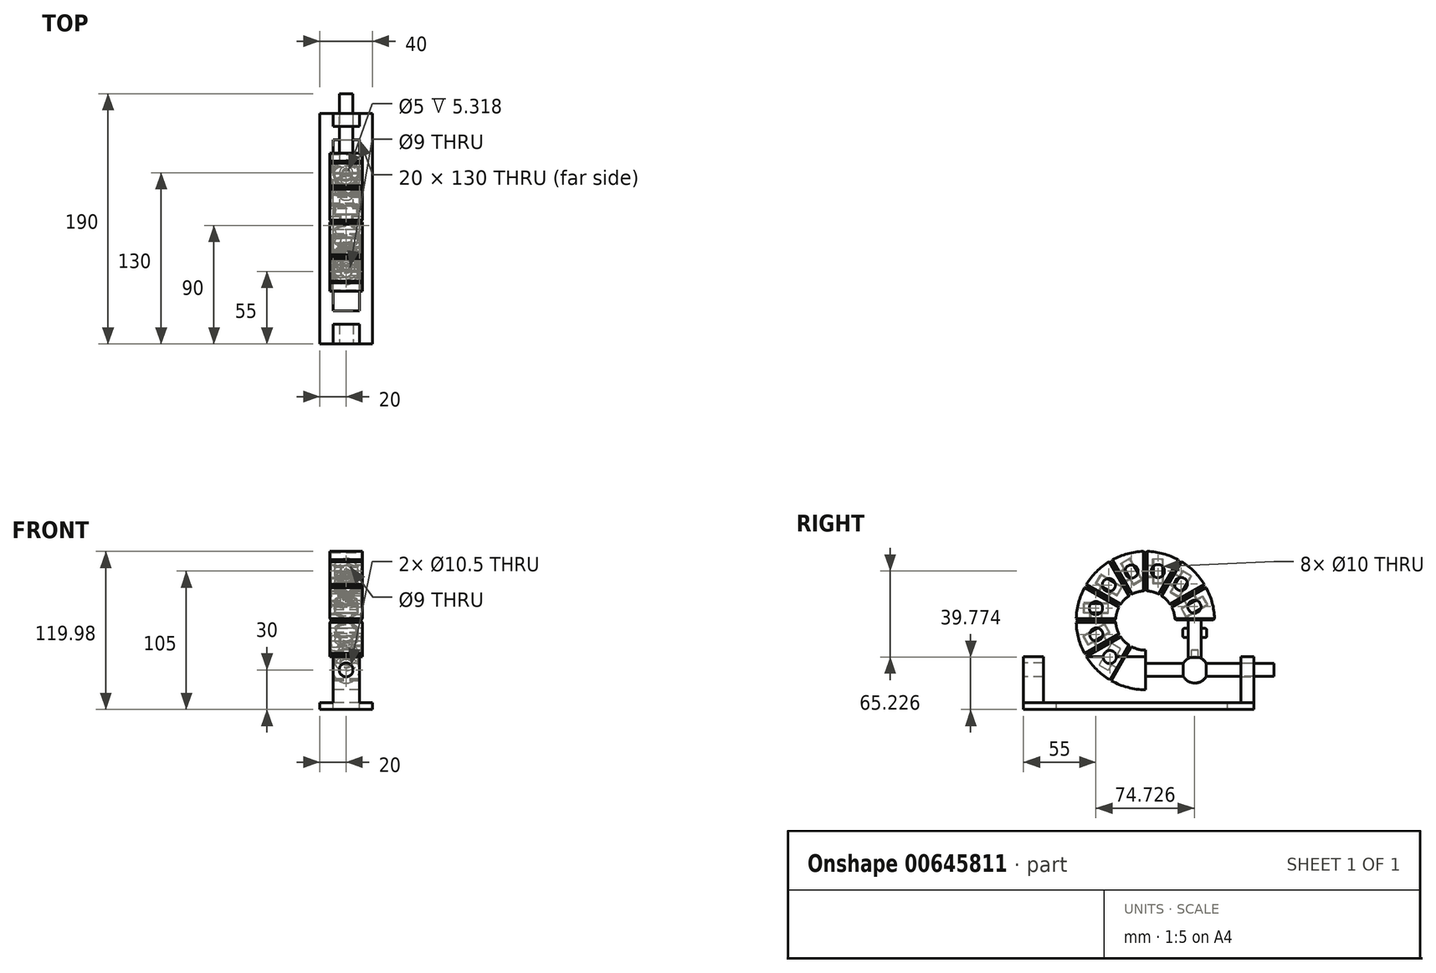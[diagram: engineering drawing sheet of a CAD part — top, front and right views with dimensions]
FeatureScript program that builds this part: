
annotation { "Feature Type Name" : "Feature", "Feature Type Description" : "" }
export const myFeature = defineFeature(function(context is Context, id is Id, definition is map)
    precondition{}
    {
        {
            var Q0;
            Q0=qCreatedBy(makeId("Right.planeOp"),FACE);
            var sketch = newSketch(context, id + "F0", { "sketchPlane" : qUnion([Q0])});
            skLineSegment(sketch, "E0", {"start": v(0, 30) * mm, "end": v(0, 0) * mm});
            skArc(sketch, "E1", {"start": v(-26.25, 7.03) * mm, "mid": v(-13.59, 1.79) * mm, "end": v(0, 0) * mm});
            skArc(sketch, "E2", {"start": v(0, 30) * mm, "mid": v(-5.82, 30.77) * mm, "end": v(-11.25, 33.01) * mm});
            skLineSegment(sketch, "E3", {"start": v(-11.25, 33.01) * mm, "end": v(-26.25, 7.03) * mm, "construction": true});
            skLineSegment(sketch, "E4", {"start": v(-16.32, 23.24) * mm, "end": v(-21.95, 26.49) * mm});
            skLineSegment(sketch, "E5", {"start": v(-25.95, 19.56) * mm, "end": v(-20.32, 16.3) * mm});
            skLineSegment(sketch, "E6", {"start": v(-25.95, 19.56) * mm, "end": v(-27.95, 16.1) * mm});
            skLineSegment(sketch, "E7", {"start": v(-29.31, 15.73) * mm, "end": v(-33.64, 18.23) * mm});
            skLineSegment(sketch, "E8", {"start": v(-34, 19.6) * mm, "end": v(-26, 33.45) * mm});
            skLineSegment(sketch, "E9", {"start": v(-24.64, 33.82) * mm, "end": v(-20.31, 31.32) * mm});
            skLineSegment(sketch, "E10", {"start": v(-19.95, 29.95) * mm, "end": v(-21.95, 26.49) * mm});
            skLineSegment(sketch, "E11", {"start": v(-18.75, 20.02) * mm, "end": v(-30.44, 26.77) * mm});
            skArc(sketch, "E12.MirrorCS", {"start": v(-19.49, 41.25) * mm, "mid": v(-15.9, 36.6) * mm, "end": v(-11.25, 33.01) * mm});
            skLineSegment(sketch, "E13.MirrorCS", {"start": v(-19.49, 41.25) * mm, "end": v(-45.47, 26.25) * mm});
            skArc(sketch, "E14.MirrorCS", {"start": v(-26.25, 7.03) * mm, "mid": v(-37.12, 15.38) * mm, "end": v(-45.47, 26.25) * mm});
            skLineSegment(sketch, "E15", {"start": v(-11.68, 33.27) * mm, "end": v(-16.43, 25.04) * mm});
            skLineSegment(sketch, "E16.MirrorCS", {"start": v(-26.69, 7.28) * mm, "end": v(-21.93, 15.51) * mm});
            skLineSegment(sketch, "E17", {"start": v(-25.82, 6.78) * mm, "end": v(-10.81, 32.77) * mm});
            skLineSegment(sketch, "E18", {"start": v(-22.3, 16.88) * mm, "end": v(-24.9, 18.38) * mm});
            skLineSegment(sketch, "E19", {"start": v(-26.26, 18.01) * mm, "end": v(-28.26, 14.55) * mm});
            skLineSegment(sketch, "E20", {"start": v(-28.26, 14.55) * mm, "end": v(-35.2, 18.55) * mm});
            skLineSegment(sketch, "E21", {"start": v(-35.2, 18.55) * mm, "end": v(-25.7, 35) * mm});
            skLineSegment(sketch, "E22", {"start": v(-25.7, 35) * mm, "end": v(-18.76, 31) * mm});
            skLineSegment(sketch, "E23", {"start": v(-18.76, 31) * mm, "end": v(-20.76, 27.54) * mm});
            skLineSegment(sketch, "E24", {"start": v(-20.4, 26.17) * mm, "end": v(-17.8, 24.67) * mm});
            skLineSegment(sketch, "E25", {"start": v(0, 52.5) * mm, "end": v(-39.54, 12.96) * mm, "construction": true});
            skArc(sketch, "E26.1.21", {"start": v(-11.25, 33.01) * mm, "mid": v(-15.9, 36.6) * mm, "end": v(-19.49, 41.25) * mm});
            skPoint(sketch, "E27.orphan", {"position": v(-16.75, 23.49) * mm});
            skPoint(sketch, "E28.orphan", {"position": v(-20.75, 16.56) * mm});
            skLineSegment(sketch, "E29.1.0", {"start": v(-37.12, 32.8) * mm, "end": v(-38.62, 35.4) * mm});
            skLineSegment(sketch, "E29.1.1", {"start": v(-39.99, 35.76) * mm, "end": v(-43.45, 33.76) * mm});
            skLineSegment(sketch, "E29.1.2", {"start": v(-43.45, 33.76) * mm, "end": v(-47.45, 40.7) * mm});
            skLineSegment(sketch, "E29.1.3", {"start": v(-47.45, 40.7) * mm, "end": v(-31, 50.2) * mm});
            skLineSegment(sketch, "E29.1.4", {"start": v(-31, 50.2) * mm, "end": v(-27, 43.26) * mm});
            skLineSegment(sketch, "E29.1.5", {"start": v(-27, 43.26) * mm, "end": v(-30.46, 41.26) * mm});
            skLineSegment(sketch, "E29.1.6", {"start": v(-30.83, 39.9) * mm, "end": v(-29.33, 37.3) * mm});
            skLineSegment(sketch, "E29.1.7", {"start": v(-19.73, 41.69) * mm, "end": v(-27.96, 36.93) * mm});
            skLineSegment(sketch, "E29.1.8", {"start": v(-45.72, 26.68) * mm, "end": v(-37.49, 31.43) * mm});
            skArc(sketch, "E29.1.9", {"start": v(-45.47, 26.25) * mm, "mid": v(-50.71, 38.91) * mm, "end": v(-52.5, 52.5) * mm});
            skArc(sketch, "E29.1.10", {"start": v(-19.49, 41.25) * mm, "mid": v(-21.73, 46.68) * mm, "end": v(-22.5, 52.5) * mm});
            skLineSegment(sketch, "E29.1.11", {"start": v(-45.22, 25.81) * mm, "end": v(-19.23, 40.82) * mm});
            skLineSegment(sketch, "E29.1.12", {"start": v(-22.5, 52.5) * mm, "end": v(-52.5, 52.5) * mm});
            skLineSegment(sketch, "E29.1.13", {"start": v(-30.68, 48.64) * mm, "end": v(-28.18, 44.31) * mm});
            skLineSegment(sketch, "E29.1.14", {"start": v(-45.9, 41) * mm, "end": v(-32.05, 49) * mm});
            skLineSegment(sketch, "E29.1.15", {"start": v(-43.77, 35.31) * mm, "end": v(-46.27, 39.64) * mm});
            skLineSegment(sketch, "E29.1.16", {"start": v(-38.94, 36.95) * mm, "end": v(-42.4, 34.95) * mm});
            skLineSegment(sketch, "E29.1.17", {"start": v(-38.94, 36.95) * mm, "end": v(-35.7, 31.32) * mm});
            skLineSegment(sketch, "E29.1.18", {"start": v(-28.76, 35.32) * mm, "end": v(-32.01, 40.95) * mm});
            skLineSegment(sketch, "E29.1.19", {"start": v(-28.55, 42.95) * mm, "end": v(-32.01, 40.95) * mm});
            skLineSegment(sketch, "E29.2.0", {"start": v(-42, 53) * mm, "end": v(-42, 58) * mm});
            skLineSegment(sketch, "E29.2.1", {"start": v(-42, 58) * mm, "end": v(-47, 58) * mm});
            skLineSegment(sketch, "E29.2.2", {"start": v(-47, 58) * mm, "end": v(-47, 66) * mm});
            skLineSegment(sketch, "E29.2.3", {"start": v(-47, 66) * mm, "end": v(-28, 66) * mm});
            skLineSegment(sketch, "E29.2.4", {"start": v(-28, 66) * mm, "end": v(-28, 58) * mm});
            skLineSegment(sketch, "E29.2.5", {"start": v(-28, 58) * mm, "end": v(-33, 58) * mm});
            skLineSegment(sketch, "E29.2.6", {"start": v(-33, 58) * mm, "end": v(-33, 53) * mm});
            skLineSegment(sketch, "E29.2.7", {"start": v(-22.5, 53) * mm, "end": v(-33, 53) * mm});
            skLineSegment(sketch, "E29.2.8", {"start": v(-52.5, 53) * mm, "end": v(-42, 53) * mm});
            skArc(sketch, "E29.2.9", {"start": v(-52.5, 52.5) * mm, "mid": v(-50.71, 66.09) * mm, "end": v(-45.47, 78.75) * mm});
            skArc(sketch, "E29.2.10", {"start": v(-22.5, 52.5) * mm, "mid": v(-21.73, 58.32) * mm, "end": v(-19.49, 63.75) * mm});
            skLineSegment(sketch, "E29.2.11", {"start": v(-52.5, 52) * mm, "end": v(-22.5, 52) * mm});
            skLineSegment(sketch, "E29.2.12", {"start": v(-19.49, 63.75) * mm, "end": v(-45.47, 78.75) * mm});
            skLineSegment(sketch, "E29.2.13", {"start": v(-28.5, 65.5) * mm, "end": v(-28.5, 58.5) * mm});
            skLineSegment(sketch, "E29.2.14", {"start": v(-46.5, 65.5) * mm, "end": v(-28.5, 65.5) * mm});
            skLineSegment(sketch, "E29.2.15", {"start": v(-46.5, 58.5) * mm, "end": v(-46.5, 65.5) * mm});
            skLineSegment(sketch, "E29.2.16", {"start": v(-41.5, 58.5) * mm, "end": v(-46.5, 58.5) * mm});
            skLineSegment(sketch, "E29.2.17", {"start": v(-41.5, 58.5) * mm, "end": v(-41.5, 52) * mm});
            skLineSegment(sketch, "E29.2.18", {"start": v(-33.5, 52) * mm, "end": v(-33.5, 58.5) * mm});
            skLineSegment(sketch, "E29.2.19", {"start": v(-28.5, 58.5) * mm, "end": v(-33.5, 58.5) * mm});
            skLineSegment(sketch, "E29.3.0", {"start": v(-36.12, 73.93) * mm, "end": v(-33.62, 78.26) * mm});
            skLineSegment(sketch, "E29.3.1", {"start": v(-33.62, 78.26) * mm, "end": v(-37.95, 80.76) * mm});
            skLineSegment(sketch, "E29.3.2", {"start": v(-37.95, 80.76) * mm, "end": v(-33.95, 87.7) * mm});
            skLineSegment(sketch, "E29.3.3", {"start": v(-33.95, 87.7) * mm, "end": v(-17.5, 78.2) * mm});
            skLineSegment(sketch, "E29.3.4", {"start": v(-17.5, 78.2) * mm, "end": v(-21.5, 71.26) * mm});
            skLineSegment(sketch, "E29.3.5", {"start": v(-21.5, 71.26) * mm, "end": v(-25.83, 73.76) * mm});
            skLineSegment(sketch, "E29.3.6", {"start": v(-25.83, 73.76) * mm, "end": v(-28.33, 69.43) * mm});
            skLineSegment(sketch, "E29.3.7", {"start": v(-19.23, 64.18) * mm, "end": v(-28.33, 69.43) * mm});
            skLineSegment(sketch, "E29.3.8", {"start": v(-45.22, 79.19) * mm, "end": v(-36.12, 73.93) * mm});
            skArc(sketch, "E29.3.9", {"start": v(-45.47, 78.75) * mm, "mid": v(-37.12, 89.62) * mm, "end": v(-26.25, 97.97) * mm});
            skArc(sketch, "E29.3.10", {"start": v(-19.49, 63.75) * mm, "mid": v(-15.9, 68.4) * mm, "end": v(-11.25, 71.99) * mm});
            skLineSegment(sketch, "E29.3.11", {"start": v(-45.72, 78.32) * mm, "end": v(-19.73, 63.31) * mm});
            skLineSegment(sketch, "E29.3.12", {"start": v(-11.25, 71.99) * mm, "end": v(-26.25, 97.97) * mm});
            skLineSegment(sketch, "E29.3.13", {"start": v(-18.18, 78) * mm, "end": v(-21.68, 71.95) * mm});
            skLineSegment(sketch, "E29.3.14", {"start": v(-33.77, 87) * mm, "end": v(-18.18, 78) * mm});
            skLineSegment(sketch, "E29.3.15", {"start": v(-37.27, 80.95) * mm, "end": v(-33.77, 87) * mm});
            skLineSegment(sketch, "E29.3.16", {"start": v(-32.94, 78.45) * mm, "end": v(-37.27, 80.95) * mm});
            skLineSegment(sketch, "E29.3.17", {"start": v(-32.94, 78.45) * mm, "end": v(-36.2, 72.82) * mm});
            skLineSegment(sketch, "E29.3.18", {"start": v(-29.26, 68.82) * mm, "end": v(-26.01, 74.45) * mm});
            skLineSegment(sketch, "E29.3.19", {"start": v(-21.68, 71.95) * mm, "end": v(-26.01, 74.45) * mm});
            skLineSegment(sketch, "E29.4.0", {"start": v(-20.57, 89.12) * mm, "end": v(-16.24, 91.62) * mm});
            skLineSegment(sketch, "E29.4.1", {"start": v(-16.24, 91.62) * mm, "end": v(-18.74, 95.95) * mm});
            skLineSegment(sketch, "E29.4.2", {"start": v(-18.74, 95.95) * mm, "end": v(-11.8, 99.95) * mm});
            skLineSegment(sketch, "E29.4.3", {"start": v(-11.8, 99.95) * mm, "end": v(-2.3, 83.5) * mm});
            skLineSegment(sketch, "E29.4.4", {"start": v(-2.3, 83.5) * mm, "end": v(-9.24, 79.5) * mm});
            skLineSegment(sketch, "E29.4.5", {"start": v(-9.24, 79.5) * mm, "end": v(-11.74, 83.83) * mm});
            skLineSegment(sketch, "E29.4.6", {"start": v(-11.74, 83.83) * mm, "end": v(-16.07, 81.33) * mm});
            skLineSegment(sketch, "E29.4.7", {"start": v(-10.81, 72.23) * mm, "end": v(-16.07, 81.33) * mm});
            skLineSegment(sketch, "E29.4.8", {"start": v(-25.82, 98.22) * mm, "end": v(-20.57, 89.12) * mm});
            skArc(sketch, "E29.4.9", {"start": v(-26.25, 97.97) * mm, "mid": v(-13.59, 103.21) * mm, "end": v(0, 105) * mm});
            skArc(sketch, "E29.4.10", {"start": v(-11.25, 71.99) * mm, "mid": v(-5.82, 74.23) * mm, "end": v(0, 75) * mm});
            skLineSegment(sketch, "E29.4.11", {"start": v(-26.69, 97.72) * mm, "end": v(-11.68, 71.73) * mm});
            skLineSegment(sketch, "E29.4.12", {"start": v(0, 75) * mm, "end": v(0, 105) * mm});
            skLineSegment(sketch, "E29.4.13", {"start": v(-3, 83.68) * mm, "end": v(-9.05, 80.18) * mm});
            skLineSegment(sketch, "E29.4.14", {"start": v(-12, 99.27) * mm, "end": v(-3, 83.68) * mm});
            skLineSegment(sketch, "E29.4.15", {"start": v(-18.05, 95.77) * mm, "end": v(-12, 99.27) * mm});
            skLineSegment(sketch, "E29.4.16", {"start": v(-15.55, 91.44) * mm, "end": v(-18.05, 95.77) * mm});
            skLineSegment(sketch, "E29.4.17", {"start": v(-15.55, 91.44) * mm, "end": v(-21.18, 88.2) * mm});
            skLineSegment(sketch, "E29.4.18", {"start": v(-17.18, 81.26) * mm, "end": v(-11.55, 84.51) * mm});
            skLineSegment(sketch, "E29.4.19", {"start": v(-9.05, 80.18) * mm, "end": v(-11.55, 84.51) * mm});
            skLineSegment(sketch, "E29.5.0", {"start": v(0.5, 94.5) * mm, "end": v(5.5, 94.5) * mm});
            skLineSegment(sketch, "E29.5.1", {"start": v(5.5, 94.5) * mm, "end": v(5.5, 99.5) * mm});
            skLineSegment(sketch, "E29.5.2", {"start": v(5.5, 99.5) * mm, "end": v(13.5, 99.5) * mm});
            skLineSegment(sketch, "E29.5.3", {"start": v(13.5, 99.5) * mm, "end": v(13.5, 80.5) * mm});
            skLineSegment(sketch, "E29.5.4", {"start": v(13.5, 80.5) * mm, "end": v(5.5, 80.5) * mm});
            skLineSegment(sketch, "E29.5.5", {"start": v(5.5, 80.5) * mm, "end": v(5.5, 85.5) * mm});
            skLineSegment(sketch, "E29.5.6", {"start": v(5.5, 85.5) * mm, "end": v(0.5, 85.5) * mm});
            skLineSegment(sketch, "E29.5.7", {"start": v(0.5, 75) * mm, "end": v(0.5, 85.5) * mm});
            skLineSegment(sketch, "E29.5.8", {"start": v(0.5, 105) * mm, "end": v(0.5, 94.5) * mm});
            skArc(sketch, "E29.5.9", {"start": v(0, 105) * mm, "mid": v(13.59, 103.21) * mm, "end": v(26.25, 97.97) * mm});
            skArc(sketch, "E29.5.10", {"start": v(0, 75) * mm, "mid": v(5.82, 74.23) * mm, "end": v(11.25, 71.99) * mm});
            skLineSegment(sketch, "E29.5.11", {"start": v(-0.5, 105) * mm, "end": v(-0.5, 75) * mm});
            skLineSegment(sketch, "E29.5.12", {"start": v(11.25, 71.99) * mm, "end": v(26.25, 97.97) * mm});
            skLineSegment(sketch, "E29.5.13", {"start": v(13, 81) * mm, "end": v(6, 81) * mm});
            skLineSegment(sketch, "E29.5.14", {"start": v(13, 99) * mm, "end": v(13, 81) * mm});
            skLineSegment(sketch, "E29.5.15", {"start": v(6, 99) * mm, "end": v(13, 99) * mm});
            skLineSegment(sketch, "E29.5.16", {"start": v(6, 94) * mm, "end": v(6, 99) * mm});
            skLineSegment(sketch, "E29.5.17", {"start": v(6, 94) * mm, "end": v(-0.5, 94) * mm});
            skLineSegment(sketch, "E29.5.18", {"start": v(-0.5, 86) * mm, "end": v(6, 86) * mm});
            skLineSegment(sketch, "E29.5.19", {"start": v(6, 81) * mm, "end": v(6, 86) * mm});
            skLineSegment(sketch, "E29.6.0", {"start": v(21.43, 88.62) * mm, "end": v(25.76, 86.12) * mm});
            skLineSegment(sketch, "E29.6.1", {"start": v(25.76, 86.12) * mm, "end": v(28.26, 90.45) * mm});
            skLineSegment(sketch, "E29.6.2", {"start": v(28.26, 90.45) * mm, "end": v(35.2, 86.45) * mm});
            skLineSegment(sketch, "E29.6.3", {"start": v(35.2, 86.45) * mm, "end": v(25.7, 70) * mm});
            skLineSegment(sketch, "E29.6.4", {"start": v(25.7, 70) * mm, "end": v(18.76, 74) * mm});
            skLineSegment(sketch, "E29.6.5", {"start": v(18.76, 74) * mm, "end": v(21.26, 78.33) * mm});
            skLineSegment(sketch, "E29.6.6", {"start": v(21.26, 78.33) * mm, "end": v(16.93, 80.83) * mm});
            skLineSegment(sketch, "E29.6.7", {"start": v(11.68, 71.73) * mm, "end": v(16.93, 80.83) * mm});
            skLineSegment(sketch, "E29.6.8", {"start": v(26.69, 97.72) * mm, "end": v(21.43, 88.62) * mm});
            skArc(sketch, "E29.6.9", {"start": v(26.25, 97.97) * mm, "mid": v(37.12, 89.62) * mm, "end": v(45.47, 78.75) * mm});
            skArc(sketch, "E29.6.10", {"start": v(11.25, 71.99) * mm, "mid": v(15.9, 68.4) * mm, "end": v(19.49, 63.75) * mm});
            skLineSegment(sketch, "E29.6.11", {"start": v(25.82, 98.22) * mm, "end": v(10.81, 72.23) * mm});
            skLineSegment(sketch, "E29.6.12", {"start": v(19.49, 63.75) * mm, "end": v(45.47, 78.75) * mm});
            skLineSegment(sketch, "E29.6.13", {"start": v(25.5, 70.68) * mm, "end": v(19.45, 74.18) * mm});
            skLineSegment(sketch, "E29.6.14", {"start": v(34.5, 86.27) * mm, "end": v(25.5, 70.68) * mm});
            skLineSegment(sketch, "E29.6.15", {"start": v(28.45, 89.77) * mm, "end": v(34.5, 86.27) * mm});
            skLineSegment(sketch, "E29.6.16", {"start": v(25.95, 85.44) * mm, "end": v(28.45, 89.77) * mm});
            skLineSegment(sketch, "E29.6.17", {"start": v(25.95, 85.44) * mm, "end": v(20.32, 88.7) * mm});
            skLineSegment(sketch, "E29.6.18", {"start": v(16.32, 81.76) * mm, "end": v(21.95, 78.51) * mm});
            skLineSegment(sketch, "E29.6.19", {"start": v(19.45, 74.18) * mm, "end": v(21.95, 78.51) * mm});
            skLineSegment(sketch, "E29.7.0", {"start": v(36.62, 73.07) * mm, "end": v(39.12, 68.74) * mm});
            skLineSegment(sketch, "E29.7.1", {"start": v(39.12, 68.74) * mm, "end": v(43.45, 71.24) * mm});
            skLineSegment(sketch, "E29.7.2", {"start": v(43.45, 71.24) * mm, "end": v(47.45, 64.3) * mm});
            skLineSegment(sketch, "E29.7.3", {"start": v(47.45, 64.3) * mm, "end": v(31, 54.8) * mm});
            skLineSegment(sketch, "E29.7.4", {"start": v(31, 54.8) * mm, "end": v(27, 61.74) * mm});
            skLineSegment(sketch, "E29.7.5", {"start": v(27, 61.74) * mm, "end": v(31.33, 64.24) * mm});
            skLineSegment(sketch, "E29.7.6", {"start": v(31.33, 64.24) * mm, "end": v(28.83, 68.57) * mm});
            skLineSegment(sketch, "E29.7.7", {"start": v(19.73, 63.31) * mm, "end": v(28.83, 68.57) * mm});
            skLineSegment(sketch, "E29.7.8", {"start": v(45.72, 78.32) * mm, "end": v(36.62, 73.07) * mm});
            skArc(sketch, "E29.7.9", {"start": v(45.47, 78.75) * mm, "mid": v(50.71, 66.09) * mm, "end": v(52.5, 52.5) * mm});
            skArc(sketch, "E29.7.10", {"start": v(19.49, 63.75) * mm, "mid": v(21.73, 58.32) * mm, "end": v(22.5, 52.5) * mm});
            skLineSegment(sketch, "E29.7.11", {"start": v(45.22, 79.19) * mm, "end": v(19.23, 64.18) * mm});
            skLineSegment(sketch, "E29.7.12", {"start": v(22.5, 52.5) * mm, "end": v(52.5, 52.5) * mm});
            skLineSegment(sketch, "E29.7.13", {"start": v(31.18, 55.5) * mm, "end": v(27.68, 61.55) * mm});
            skLineSegment(sketch, "E29.7.14", {"start": v(46.77, 64.5) * mm, "end": v(31.18, 55.5) * mm});
            skLineSegment(sketch, "E29.7.15", {"start": v(43.27, 70.55) * mm, "end": v(46.77, 64.5) * mm});
            skLineSegment(sketch, "E29.7.16", {"start": v(38.94, 68.05) * mm, "end": v(43.27, 70.55) * mm});
            skLineSegment(sketch, "E29.7.17", {"start": v(38.94, 68.05) * mm, "end": v(35.7, 73.68) * mm});
            skLineSegment(sketch, "E29.7.18", {"start": v(28.76, 69.68) * mm, "end": v(32.01, 64.05) * mm});
            skLineSegment(sketch, "E29.7.19", {"start": v(27.68, 61.55) * mm, "end": v(32.01, 64.05) * mm});
            skLineSegment(sketch, "E29.anchor1", {"start": v(0, 52.5) * mm, "end": v(-25.76, 18.88) * mm, "construction": true});
            skLineSegment(sketch, "E29.anchor2", {"start": v(0, 52.5) * mm, "end": v(39.12, 68.74) * mm, "construction": true});
            skLineSegment(sketch, "E30", {"start": v(0, 20) * mm, "end": v(40, 20) * mm});
            skLineSegment(sketch, "E31", {"start": v(40, 20) * mm, "end": v(40, 10) * mm});
            skLineSegment(sketch, "E32", {"start": v(40, 10) * mm, "end": v(0, 10) * mm});
            skLineSegment(sketch, "E33", {"start": v(32.5, 53) * mm, "end": v(32.5, 25) * mm});
            skLineSegment(sketch, "E34", {"start": v(32.5, 25) * mm, "end": v(42.5, 25) * mm, "construction": true});
            skLineSegment(sketch, "E35", {"start": v(42.5, 25) * mm, "end": v(42.5, 53) * mm});
            skLineSegment(sketch, "E36", {"start": v(0, 15) * mm, "end": v(40, 15) * mm});
            skPoint(sketch, "E36.endSnap0", {"position": v(0, 15) * mm});
            skLineSegment(sketch, "E37", {"start": v(37.5, 53) * mm, "end": v(37.5, 15) * mm});
            skLineSegment(sketch, "E38", {"start": v(-18.75, 20.02) * mm, "end": v(-18.32, 19.77) * mm});
            skLineSegment(sketch, "E39", {"start": v(-17.18, 23.74) * mm, "end": v(-21.18, 16.8) * mm});
            skLineSegment(sketch, "E40", {"start": v(-32.23, 33.32) * mm, "end": v(-38.98, 45) * mm});
            skPoint(sketch, "E41.visualSharp", {"position": v(-34.5, 18.73) * mm});
            skArc(sketch, "E41.filletArc", {"start": v(-34, 19.6) * mm, "mid": v(-34.1, 18.84) * mm, "end": v(-33.64, 18.23) * mm});
            skPoint(sketch, "E42.visualSharp", {"position": v(-25.5, 34.32) * mm});
            skArc(sketch, "E42.filletArc", {"start": v(-24.64, 33.82) * mm, "mid": v(-25.4, 33.92) * mm, "end": v(-26, 33.45) * mm});
            skPoint(sketch, "E43.visualSharp", {"position": v(-19.45, 30.82) * mm});
            skArc(sketch, "E43.filletArc", {"start": v(-19.95, 29.95) * mm, "mid": v(-19.85, 30.71) * mm, "end": v(-20.31, 31.32) * mm});
            skPoint(sketch, "E44.visualSharp", {"position": v(-28.45, 15.23) * mm});
            skArc(sketch, "E44.filletArc", {"start": v(-29.31, 15.73) * mm, "mid": v(-28.55, 15.63) * mm, "end": v(-27.95, 16.1) * mm});
            skPoint(sketch, "E45.visualSharp", {"position": v(-21.26, 26.67) * mm});
            skArc(sketch, "E45.filletArc", {"start": v(-20.76, 27.54) * mm, "mid": v(-20.86, 26.78) * mm, "end": v(-20.4, 26.17) * mm});
            skPoint(sketch, "E46.visualSharp", {"position": v(-25.76, 18.88) * mm});
            skArc(sketch, "E46.filletArc", {"start": v(-24.9, 18.38) * mm, "mid": v(-25.66, 18.48) * mm, "end": v(-26.26, 18.01) * mm});
            skPoint(sketch, "E47.visualSharp", {"position": v(-46.77, 40.5) * mm});
            skArc(sketch, "E47.filletArc", {"start": v(-45.9, 41) * mm, "mid": v(-46.37, 40.4) * mm, "end": v(-46.27, 39.64) * mm});
            skPoint(sketch, "E48.visualSharp", {"position": v(-31.18, 49.5) * mm});
            skArc(sketch, "E48.filletArc", {"start": v(-30.68, 48.64) * mm, "mid": v(-31.29, 49.1) * mm, "end": v(-32.05, 49) * mm});
            skPoint(sketch, "E49.visualSharp", {"position": v(-27.68, 43.45) * mm});
            skArc(sketch, "E49.filletArc", {"start": v(-28.55, 42.95) * mm, "mid": v(-28.08, 43.55) * mm, "end": v(-28.18, 44.31) * mm});
            skPoint(sketch, "E50.visualSharp", {"position": v(-31.33, 40.76) * mm});
            skArc(sketch, "E50.filletArc", {"start": v(-30.46, 41.26) * mm, "mid": v(-30.93, 40.66) * mm, "end": v(-30.83, 39.9) * mm});
            skPoint(sketch, "E51.visualSharp", {"position": v(-39.12, 36.26) * mm});
            skArc(sketch, "E51.filletArc", {"start": v(-38.62, 35.4) * mm, "mid": v(-39.23, 35.86) * mm, "end": v(-39.99, 35.76) * mm});
            skPoint(sketch, "E52.visualSharp", {"position": v(-43.27, 34.45) * mm});
            skArc(sketch, "E52.filletArc", {"start": v(-43.77, 35.31) * mm, "mid": v(-43.16, 34.85) * mm, "end": v(-42.4, 34.95) * mm});
            skLineSegment(sketch, "E53", {"start": v(22.5, 53) * mm, "end": v(52.5, 53) * mm});
            skPoint(sketch, "E54.visualSharp", {"position": v(-36.62, 31.93) * mm});
            skArc(sketch, "E54.filletArc", {"start": v(-37.49, 31.43) * mm, "mid": v(-37.02, 32.04) * mm, "end": v(-37.12, 32.8) * mm});
            skPoint(sketch, "E55.visualSharp", {"position": v(-28.83, 36.43) * mm});
            skArc(sketch, "E55.filletArc", {"start": v(-29.33, 37.3) * mm, "mid": v(-28.72, 36.83) * mm, "end": v(-27.96, 36.93) * mm});
            skPoint(sketch, "E56.visualSharp", {"position": v(-21.43, 16.38) * mm});
            skArc(sketch, "E56.filletArc", {"start": v(-21.93, 15.51) * mm, "mid": v(-21.83, 16.27) * mm, "end": v(-22.3, 16.88) * mm});
            skPoint(sketch, "E57.visualSharp", {"position": v(-16.93, 24.17) * mm});
            skArc(sketch, "E57.filletArc", {"start": v(-17.8, 24.67) * mm, "mid": v(-17.04, 24.57) * mm, "end": v(-16.43, 25.04) * mm});
            skLineSegment(sketch, "E58", {"start": v(-21.93, 15.51) * mm, "end": v(-21.18, 16.8) * mm});
            skLineSegment(sketch, "E59", {"start": v(-17.18, 23.74) * mm, "end": v(-16.43, 25.04) * mm});
            skLineSegment(sketch, "E60", {"start": v(22.5, 52.5) * mm, "end": v(32.5, 52.5) * mm});
            skLineSegment(sketch, "E61", {"start": v(42.5, 52.5) * mm, "end": v(52.5, 52.5) * mm});
            skLineSegment(sketch, "E62", {"start": v(0, 20) * mm, "end": v(0, 30) * mm});
            skLineSegment(sketch, "E63", {"start": v(0, 10) * mm, "end": v(0, 0) * mm});
            skLineSegment(sketch, "E64", {"start": v(37.5, 15) * mm, "end": v(40, 15) * mm, "construction": true});
            skArc(sketch, "E65", {"start": v(37.5, 25) * mm, "mid": v(47.5, 15) * mm, "end": v(37.5, 5) * mm});
            skLineSegment(sketch, "E66", {"start": v(37.5, 15) * mm, "end": v(37.5, 5) * mm});
            skLineSegment(sketch, "E67", {"start": v(0, 30) * mm, "end": v(40, 30) * mm});
            skLineSegment(sketch, "E68", {"start": v(40, 30) * mm, "end": v(40, 20) * mm});
            skLineSegment(sketch, "E69", {"start": v(32.5, 25) * mm, "end": v(32.5, 24.5) * mm});
            skLineSegment(sketch, "E70", {"start": v(32.5, 24.5) * mm, "end": v(42.5, 24.5) * mm});
            skLineSegment(sketch, "E71", {"start": v(42.5, 24.5) * mm, "end": v(42.5, 25) * mm});
            skLineSegment(sketch, "E72", {"start": v(52.5, 52.5) * mm, "end": v(52.5, 38.27) * mm});
            skLineSegment(sketch, "E73", {"start": v(52.5, 38.27) * mm, "end": v(22.5, 38.27) * mm});
            skLineSegment(sketch, "E74", {"start": v(22.5, 38.27) * mm, "end": v(22.5, 52.5) * mm});
            skPoint(sketch, "E75.orphan", {"position": v(37.5, 52.5) * mm});
            skSolve(sketch);
        }
        {
            var Q0;
            {var subQ1=sQuery(id+"F0.wireOp",EDGE,"E0");var subQ9=sQuery(id+"F0.wireOp",EDGE,"E2");var subQ10=makeQuery(id+"F0.imprint","INTERSECT",VERTEX,{"derivedFrom":[subQ1,subQ9]});Q0=makeQuery(id+"F0.imprint","IMPRINT",FACE,{"disambiguationData":[TD([[makeQuery(id+"F0.imprint","IMPRINT",EDGE,{"disambiguationData":[TD([[subQ10,-1.0]])],"derivedFrom":subQ1}),-1.0]])]});}
            extrude(context, id + "F1", {"entities" : qUnion([Q0]), "endBound" : BoundingType.SYMMETRIC, "depth" : 25 * mm, "offsetDistance" : 25 * mm, "hasSecondDirection" : true, "secondDirectionOppositeDirection" : true, "secondDirectionDepth" : 20 * mm});
        }
        {
            var Q0;
            {var subQ2=sQuery(id+"F0.wireOp",EDGE,"E4");Q0=makeQuery(id+"F0.imprint","IMPRINT",FACE,{"disambiguationData":[TD([[makeQuery(id+"F0.imprint","IMPRINT",EDGE,{"derivedFrom":subQ2}),1.0]])]});}
            var Q1;
            {var subQ1=sQuery(id+"F0.wireOp",EDGE,"E9");Q1=makeQuery(id+"F0.imprint","IMPRINT",FACE,{"disambiguationData":[TD([[makeQuery(id+"F0.imprint","IMPRINT",EDGE,{"derivedFrom":subQ1}),-1.0]])]});}
            var Q2;
            Q2=sQuery(id+"F0.wireOp",EDGE,"E11");
            revolve(context, id + "F2", {"operationType" : NewBodyOperationType.ADD, "entities" : qUnion([Q0, Q1]), "axis" : qUnion([Q2]), "revolveType" : RevolveType.FULL});
        }
        {
            var Q0;
            {var subQ0=sQuery(id+"F0.wireOp",EDGE,"E30");Q0=makeQuery(id+"F0.imprint","IMPRINT",FACE,{"disambiguationData":[TD([[makeQuery(id+"F0.imprint","IMPRINT",EDGE,{"derivedFrom":subQ0}),-1.0]])]});}
            var Q1;
            Q1=sQuery(id+"F0.wireOp",EDGE,"E36");
            revolve(context, id + "F3", {"operationType" : NewBodyOperationType.ADD, "entities" : qUnion([Q0]), "axis" : qUnion([Q1]), "revolveType" : RevolveType.FULL});
        }
        {
            var Q0;
            {var subQ7=sQuery(id+"F0.wireOp",EDGE,"E15");Q0=makeQuery(id+"F0.imprint","IMPRINT",FACE,{"disambiguationData":[TD([[makeQuery(id+"F0.imprint","IMPRINT",EDGE,{"derivedFrom":subQ7}),-1.0]])]});}
            var Q1;
            {var subQ2=sQuery(id+"F0.wireOp",EDGE,"E9");Q1=makeQuery(id+"F0.imprint","IMPRINT",FACE,{"disambiguationData":[TD([[makeQuery(id+"F0.imprint","IMPRINT",EDGE,{"derivedFrom":subQ2}),1.0]])]});}
            var Q2;
            {var subQ1=sQuery(id+"F0.wireOp",EDGE,"E9");Q2=makeQuery(id+"F0.imprint","IMPRINT",FACE,{"disambiguationData":[TD([[makeQuery(id+"F0.imprint","IMPRINT",EDGE,{"derivedFrom":subQ1}),-1.0]])]});}
            var Q3;
            {var subQ4=sQuery(id+"F0.wireOp",EDGE,"E6");Q3=makeQuery(id+"F0.imprint","IMPRINT",FACE,{"disambiguationData":[TD([[makeQuery(id+"F0.imprint","IMPRINT",EDGE,{"derivedFrom":subQ4}),-1.0]])]});}
            var Q4;
            {var subQ7=sQuery(id+"F0.wireOp",EDGE,"E6");Q4=makeQuery(id+"F0.imprint","IMPRINT",FACE,{"disambiguationData":[TD([[makeQuery(id+"F0.imprint","IMPRINT",EDGE,{"derivedFrom":subQ7}),1.0]])]});}
            extrude(context, id + "F4", {"entities" : qUnion([Q0, Q1, Q2, Q3, Q4]), "endBound" : BoundingType.SYMMETRIC, "depth" : 25 * mm, "offsetDistance" : 25 * mm, "hasSecondDirection" : true, "secondDirectionOppositeDirection" : true, "secondDirectionDepth" : 20 * mm});
        }
        {
            var Q0;
            Q0=makeQuery(id+"F4.opExtrude","CAP_FACE",FACE,{"disambiguationData":[OSD([sQuery(id+"F0.wireOp",EDGE,"E14.MirrorCS"),sQuery(id+"F0.wireOp",EDGE,"E15"),sQuery(id+"F0.wireOp",EDGE,"E16.MirrorCS"),sQuery(id+"F0.wireOp",EDGE,"E26.1.21"),sQuery(id+"F0.wireOp",EDGE,"E29.1.11"),sQuery(id+"F0.wireOp",EDGE,"E39")])],"isStart":false});
            var sketch = newSketch(context, id + "F5", { "sketchPlane" : qUnion([Q0])});
            skPoint(sketch, "E76", {"position": v(-26.98, 24.77) * mm});
            skSolve(sketch);
        }
        {
            var Q0;
            Q0=sQuery(id+"F5.wireOp",VERTEX,"E76");
            var Q1;
            Q1=makeQuery(id+"F4.opExtrude","SWEPT_BODY",BODY,{"disambiguationData":[OSD([sQuery(id+"F0.wireOp",EDGE,"E14.MirrorCS"),sQuery(id+"F0.wireOp",EDGE,"E15"),sQuery(id+"F0.wireOp",EDGE,"E16.MirrorCS"),sQuery(id+"F0.wireOp",EDGE,"E26.1.21"),sQuery(id+"F0.wireOp",EDGE,"E29.1.11"),sQuery(id+"F0.wireOp",EDGE,"E39")])]});
            hole(context, id + "F6", {"style" : HoleStyle.SIMPLE, "endStyle" : HoleEndStyle.THROUGH, "holeDiameter" : 10 * mm, "majorDiameter" : 5 * mm, "isTappedThrough" : true, "tappedDepth" : 12 * mm, "tapClearance" : 3, "locations" : qUnion([Q0]), "scope" : qUnion([Q1])});
        }
        {
            var Q0;
            Q0=sQuery(id+"F0.wireOp",EDGE,"E7");
            cPoint(context, id + "F7", {"entities" : qUnion([Q0]), "parameter" : 0.5});
        }
        {
            var Q0;
            Q0 = qCreatedBy(id + "F7" ,VERTEX);
            var Q1;
            Q1=sQuery(id+"F0.wireOp",EDGE,"E21");
            cPlane(context, id + "F8", {"entities" : qUnion([Q0, Q1]), "cplaneType" : CPlaneType.LINE_POINT, "offset" : 25 * mm, "width" : 150 * mm, "height" : 150 * mm});
        }
        {
            var Q0;
            Q0=qCreatedBy(id+"F8.planeOp",FACE);
            var sketch = newSketch(context, id + "F9", { "sketchPlane" : qUnion([Q0])});
            skPoint(sketch, "E77", {"position": v(0, -35.26) * mm});
            skSolve(sketch);
        }
        {
            var Q0;
            Q0=makeQuery(id+"F4.opExtrude","CAP_EDGE",EDGE,{"disambiguationData":[OSD([sQuery(id+"F0.wireOp",EDGE,"E15"),sQuery(id+"F0.wireOp",EDGE,"E16.MirrorCS"),sQuery(id+"F0.wireOp",EDGE,"E39")])],"isStart":true});
            var Q1;
            Q1=makeQuery(id+"F4.opExtrude","SWEPT_EDGE",EDGE,{"disambiguationData":[OSD([sQuery(id+"F0.wireOp",EDGE,"E15"),sQuery(id+"F0.wireOp",EDGE,"E26.1.21")])]});
            var Q2;
            Q2=makeQuery(id+"F4.opExtrude","CAP_EDGE",EDGE,{"disambiguationData":[OSD([sQuery(id+"F0.wireOp",EDGE,"E15"),sQuery(id+"F0.wireOp",EDGE,"E16.MirrorCS"),sQuery(id+"F0.wireOp",EDGE,"E39")])],"isStart":false});
            var Q3;
            Q3=makeQuery(id+"F4.opExtrude","SWEPT_EDGE",EDGE,{"disambiguationData":[OSD([sQuery(id+"F0.wireOp",EDGE,"E14.MirrorCS"),sQuery(id+"F0.wireOp",EDGE,"E16.MirrorCS")])]});
            var Q4;
            Q4=makeQuery(id+"F4.opExtrude","CAP_EDGE",EDGE,{"disambiguationData":[OSD([sQuery(id+"F0.wireOp",EDGE,"E29.1.11")])],"isStart":true});
            var Q5;
            Q5=makeQuery(id+"F4.opExtrude","SWEPT_EDGE",EDGE,{"disambiguationData":[OSD([sQuery(id+"F0.wireOp",EDGE,"E14.MirrorCS"),sQuery(id+"F0.wireOp",EDGE,"E29.1.11")])]});
            var Q6;
            Q6=makeQuery(id+"F4.opExtrude","CAP_EDGE",EDGE,{"disambiguationData":[OSD([sQuery(id+"F0.wireOp",EDGE,"E29.1.11")])],"isStart":false});
            var Q7;
            Q7=makeQuery(id+"F4.opExtrude","SWEPT_EDGE",EDGE,{"disambiguationData":[OSD([sQuery(id+"F0.wireOp",EDGE,"E26.1.21"),sQuery(id+"F0.wireOp",EDGE,"E29.1.11")])]});
            chamfer(context, id + "F10", {"entities" : qUnion([Q0, Q1, Q2, Q3, Q4, Q5, Q6, Q7]), "width" : 1 * mm, "tangentPropagation" : true});
        }
        {
            var Q0;
            {var subQ1=sQuery(id+"F0.wireOp",EDGE,"E29.1.13");Q0=makeQuery(id+"F0.imprint","IMPRINT",FACE,{"disambiguationData":[TD([[makeQuery(id+"F0.imprint","IMPRINT",EDGE,{"derivedFrom":subQ1}),-1.0]])]});}
            var Q1;
            {var subQ0=sQuery(id+"F0.wireOp",EDGE,"E29.1.18");var subQ1=sQuery(id+"F0.wireOp",EDGE,"E13.MirrorCS");var subQ2=makeQuery(id+"F0.imprint","INTERSECT",VERTEX,{"derivedFrom":[subQ1,subQ0]});Q1=makeQuery(id+"F0.imprint","IMPRINT",FACE,{"disambiguationData":[TD([[makeQuery(id+"F0.imprint","IMPRINT",EDGE,{"disambiguationData":[TD([[subQ2,-1.0]])],"derivedFrom":subQ1}),1.0]])]});}
            var Q2;
            Q2=sQuery(id+"F0.wireOp",EDGE,"E40");
            revolve(context, id + "F11", {"operationType" : NewBodyOperationType.ADD, "entities" : qUnion([Q0, Q1]), "axis" : qUnion([Q2]), "revolveType" : RevolveType.FULL});
        }
        {
            var Q0;
            {var subQ1=sQuery(id+"F0.wireOp",EDGE,"E9");Q0=makeQuery(id+"F0.imprint","IMPRINT",FACE,{"disambiguationData":[TD([[makeQuery(id+"F0.imprint","IMPRINT",EDGE,{"derivedFrom":subQ1}),-1.0]])]});}
            var Q1;
            {var subQ2=sQuery(id+"F0.wireOp",EDGE,"E9");Q1=makeQuery(id+"F0.imprint","IMPRINT",FACE,{"disambiguationData":[TD([[makeQuery(id+"F0.imprint","IMPRINT",EDGE,{"derivedFrom":subQ2}),1.0]])]});}
            var Q2;
            Q2=sQuery(id+"F0.wireOp",EDGE,"E11");
            revolve(context, id + "F12", {"operationType" : NewBodyOperationType.REMOVE, "entities" : qUnion([Q0, Q1]), "axis" : qUnion([Q2]), "revolveType" : RevolveType.FULL, "oppositeDirection" : true});
        }
        {
            var Q0;
            Q0=qCreatedBy(makeId("Right.planeOp"),FACE);
            var sketch = newSketch(context, id + "F13", { "sketchPlane" : qUnion([Q0])});
            skLineSegment(sketch, "E78", {"start": v(-20.55, 19.9) * mm, "end": v(-18.82, 18.9) * mm});
            skLineSegment(sketch, "E79", {"start": v(-18.82, 18.9) * mm, "end": v(-17.82, 20.64) * mm});
            skLineSegment(sketch, "E80", {"start": v(-17.82, 20.64) * mm, "end": v(-19.55, 21.64) * mm});
            skLineSegment(sketch, "E81", {"start": v(-19.55, 21.64) * mm, "end": v(-20.55, 19.9) * mm});
            skSolve(sketch);
        }
        {
            var Q0;
            Q0=makeQuery(id+"F4.opExtrude","SWEPT_BODY",BODY,{"disambiguationData":[OSD([sQuery(id+"F0.wireOp",EDGE,"E15"),sQuery(id+"F0.wireOp",EDGE,"E16.MirrorCS"),sQuery(id+"F0.wireOp",EDGE,"E26.1.20"),sQuery(id+"F0.wireOp",EDGE,"E26.1.21"),sQuery(id+"F0.wireOp",EDGE,"E29.1.11"),sQuery(id+"F0.wireOp",EDGE,"E39")])]});
            var Q1;
            Q1=makeQuery(id+"F1.opExtrude","SWEPT_FACE",FACE,{"disambiguationData":[OSD([sQuery(id+"F0.wireOp",EDGE,"E2")])]});
            circularPattern(context, id + "F14", {"entities" : qUnion([Q0]), "axis" : qUnion([Q1]), "angle" : 210 * degree, "instanceCount" : 8, "oppositeDirection" : true, "equalSpace" : true});
        }
        {
            var Q0;
            {var subQ0=sQuery(id+"F0.wireOp",EDGE,"E35");Q0=makeQuery(id+"F0.imprint","IMPRINT",FACE,{"disambiguationData":[TD([[makeQuery(id+"F0.imprint","IMPRINT",EDGE,{"derivedFrom":subQ0}),1.0]])]});}
            var Q1;
            {var subQ0=sQuery(id+"F0.wireOp",EDGE,"E33");Q1=makeQuery(id+"F0.imprint","IMPRINT",FACE,{"disambiguationData":[TD([[makeQuery(id+"F0.imprint","IMPRINT",EDGE,{"derivedFrom":subQ0}),1.0]])]});}
            var Q2;
            {var subQ6=sQuery(id+"F0.wireOp",EDGE,"E53");Q2=makeQuery(id+"F0.imprint","IMPRINT",FACE,{"disambiguationData":[TD([[makeQuery(id+"F0.imprint","IMPRINT",EDGE,{"derivedFrom":subQ6}),-1.0]])]});}
            var Q3;
            {var subQ0=sQuery(id+"F0.wireOp",EDGE,"E61");Q3=makeQuery(id+"F0.imprint","IMPRINT",FACE,{"disambiguationData":[TD([[makeQuery(id+"F0.imprint","IMPRINT",EDGE,{"derivedFrom":subQ0}),-1.0]])]});}
            var Q4;
            {var subQ0=sQuery(id+"F0.wireOp",EDGE,"E60");Q4=makeQuery(id+"F0.imprint","IMPRINT",FACE,{"disambiguationData":[TD([[makeQuery(id+"F0.imprint","IMPRINT",EDGE,{"derivedFrom":subQ0}),-1.0]])]});}
            var Q5;
            {var subQ3=sQuery(id+"F0.wireOp",EDGE,"E53");var subQ5=sQuery(id+"F0.wireOp",EDGE,"E33");var subQ8=makeQuery(id+"F0.imprint","INTERSECT",VERTEX,{"derivedFrom":[subQ5,subQ3]});Q5=makeQuery(id+"F0.imprint","IMPRINT",FACE,{"disambiguationData":[TD([[makeQuery(id+"F0.imprint","IMPRINT",EDGE,{"disambiguationData":[TD([[subQ8,-1.0]])],"derivedFrom":subQ3}),-1.0]])]});}
            extrude(context, id + "F15", {"entities" : qUnion([Q0, Q1, Q2, Q3, Q4, Q5]), "operationType" : NewBodyOperationType.REMOVE, "endBound" : BoundingType.SYMMETRIC, "oppositeDirection" : true, "depth" : 30 * mm, "offsetDistance" : 25 * mm, "hasSecondDirection" : true, "secondDirectionBound" : SecondDirectionBoundingType.UP_TO_NEXT, "secondDirectionOppositeDirection" : false, "secondDirectionDepth" : 25 * mm});
        }
        {
            var Q0;
            {var subQ0=sQuery(id+"F0.wireOp",EDGE,"E66");Q0=makeQuery(id+"F0.imprint","IMPRINT",FACE,{"disambiguationData":[TD([[makeQuery(id+"F0.imprint","IMPRINT",EDGE,{"derivedFrom":subQ0}),1.0]])]});}
            var Q1;
            {var subQ0=sQuery(id+"F0.wireOp",EDGE,"E65");var subQ1=sQuery(id+"F0.wireOp",EDGE,"E37");var subQ2=makeQuery(id+"F0.imprint","INTERSECT",VERTEX,{"derivedFrom":[subQ1,subQ0]});Q1=makeQuery(id+"F0.imprint","IMPRINT",FACE,{"disambiguationData":[TD([[makeQuery(id+"F0.imprint","IMPRINT",EDGE,{"disambiguationData":[TD([[subQ2,-1.0]])],"derivedFrom":subQ1}),1.0]])]});}
            var Q2;
            {var subQ1=sQuery(id+"F0.wireOp",EDGE,"E30");var subQ3=sQuery(id+"F0.wireOp",EDGE,"E37");var subQ4=makeQuery(id+"F0.imprint","INTERSECT",VERTEX,{"derivedFrom":[subQ1,subQ3]});Q2=makeQuery(id+"F0.imprint","IMPRINT",FACE,{"disambiguationData":[TD([[makeQuery(id+"F0.imprint","IMPRINT",EDGE,{"disambiguationData":[TD([[subQ4,1.0]])],"derivedFrom":subQ3}),1.0]])]});}
            var Q3;
            {var subQ5=sQuery(id+"F0.wireOp",EDGE,"E32");var subQ6=sQuery(id+"F0.wireOp",EDGE,"E31");var subQ7=makeQuery(id+"F0.imprint","INTERSECT",VERTEX,{"derivedFrom":[subQ6,subQ5]});Q3=makeQuery(id+"F0.imprint","IMPRINT",FACE,{"disambiguationData":[TD([[makeQuery(id+"F0.imprint","IMPRINT",EDGE,{"disambiguationData":[TD([[subQ7,1.0]])],"derivedFrom":subQ6}),1.0]])]});}
            var Q4;
            {var subQ1=sQuery(id+"F0.wireOp",EDGE,"E30");var subQ3=sQuery(id+"F0.wireOp",EDGE,"E37");var subQ4=makeQuery(id+"F0.imprint","INTERSECT",VERTEX,{"derivedFrom":[subQ1,subQ3]});Q4=makeQuery(id+"F0.imprint","IMPRINT",FACE,{"disambiguationData":[TD([[makeQuery(id+"F0.imprint","IMPRINT",EDGE,{"disambiguationData":[TD([[subQ4,-1.0]])],"derivedFrom":subQ1}),-1.0]])]});}
            var Q5;
            {var subQ0=sQuery(id+"F0.wireOp",EDGE,"E70");var subQ1=sQuery(id+"F0.wireOp",EDGE,"E65");var subQ2=makeQuery(id+"F0.imprint","INTERSECT",VERTEX,{"derivedFrom":[subQ1,subQ0]});Q5=makeQuery(id+"F0.imprint","IMPRINT",FACE,{"disambiguationData":[TD([[makeQuery(id+"F0.imprint","IMPRINT",EDGE,{"disambiguationData":[TD([[subQ2,1.0]])],"derivedFrom":subQ1}),-1.0]])]});}
            var Q6;
            Q6=sQuery(id+"F0.wireOp",EDGE,"E37");
            revolve(context, id + "F16", {"entities" : qUnion([Q0, Q1, Q2, Q3, Q4, Q5]), "axis" : qUnion([Q6]), "revolveType" : RevolveType.FULL});
        }
        {
            var Q0;
            Q0=makeQuery(id+"F0.imprint","IMPRINT",FACE,{"disambiguationData":[TD([[makeQuery(id+"F0.imprint","IMPRINT",EDGE,{"derivedFrom":sQuery(id+"F0.wireOp",EDGE,"E30")}),1.0]])]});
            var Q1;
            Q1=sQuery(id+"F0.wireOp",EDGE,"E64");
            revolve(context, id + "F17", {"entities" : qUnion([Q0]), "axis" : qUnion([Q1]), "revolveType" : RevolveType.FULL});
        }
        {
            var Q0;
            {var subQ0=sQuery(id+"F0.wireOp",EDGE,"E35");Q0=makeQuery(id+"F0.imprint","IMPRINT",FACE,{"disambiguationData":[TD([[makeQuery(id+"F0.imprint","IMPRINT",EDGE,{"derivedFrom":subQ0}),1.0]])]});}
            var Q1;
            {var subQ0=sQuery(id+"F0.wireOp",EDGE,"E71");var subQ3=sQuery(id+"F0.wireOp",EDGE,"E65");var subQ5=makeQuery(id+"F0.imprint","INTERSECT",VERTEX,{"derivedFrom":[subQ3,subQ0]});Q1=makeQuery(id+"F0.imprint","IMPRINT",FACE,{"disambiguationData":[TD([[makeQuery(id+"F0.imprint","IMPRINT",EDGE,{"disambiguationData":[TD([[subQ5,1.0]])],"derivedFrom":subQ3}),1.0]])]});}
            var Q2;
            {var subQ5=sQuery(id+"F0.wireOp",EDGE,"E71");Q2=makeQuery(id+"F0.imprint","IMPRINT",FACE,{"disambiguationData":[TD([[makeQuery(id+"F0.imprint","IMPRINT",EDGE,{"derivedFrom":subQ5}),1.0]])]});}
            var Q3;
            Q3=sQuery(id+"F0.wireOp",EDGE,"E37");
            revolve(context, id + "F18", {"operationType" : NewBodyOperationType.ADD, "entities" : qUnion([Q0, Q1, Q2]), "axis" : qUnion([Q3]), "revolveType" : RevolveType.FULL});
        }
        {
            var Q0;
            Q0=qCreatedBy(makeId("Right.planeOp"),FACE);
            var sketch = newSketch(context, id + "F19", { "sketchPlane" : qUnion([Q0])});
            skLineSegment(sketch, "E82.top", {"start": v(82.5, -15) * mm, "end": v(-92.5, -15) * mm});
            skLineSegment(sketch, "E83", {"start": v(-77.5, -10) * mm, "end": v(-77.5, 25) * mm});
            skLineSegment(sketch, "E84", {"start": v(-77.5, 25) * mm, "end": v(-92.5, 25) * mm});
            skLineSegment(sketch, "E85", {"start": v(-92.5, 25) * mm, "end": v(-92.5, -15) * mm});
            skPoint(sketch, "E86", {"position": v(-92.5, 15) * mm});
            skLineSegment(sketch, "E87", {"start": v(72.5, -10) * mm, "end": v(72.5, 25) * mm});
            skLineSegment(sketch, "E88", {"start": v(72.5, 25) * mm, "end": v(82.5, 25) * mm});
            skLineSegment(sketch, "E89", {"start": v(82.5, 25) * mm, "end": v(82.5, -15) * mm});
            skLineSegment(sketch, "E90.trimOffspring", {"start": v(72.5, -10) * mm, "end": v(-77.5, -10) * mm});
            skLineSegment(sketch, "E91.bottom", {"start": v(37.5, 20) * mm, "end": v(97.5, 20) * mm});
            skLineSegment(sketch, "E91.top", {"start": v(37.5, 15) * mm, "end": v(97.5, 15) * mm});
            skLineSegment(sketch, "E91.left", {"start": v(37.5, 20) * mm, "end": v(37.5, 15) * mm});
            skLineSegment(sketch, "E91.right", {"start": v(97.5, 20) * mm, "end": v(97.5, 15) * mm});
            skPoint(sketch, "E92", {"position": v(82.5, 15) * mm});
            skSolve(sketch);
        }
        {
            var Q0;
            {var subQ5=sQuery(id+"F19.wireOp",EDGE,"E91.left");Q0=makeQuery(id+"F19.imprint","IMPRINT",FACE,{"disambiguationData":[TD([[makeQuery(id+"F19.imprint","IMPRINT",EDGE,{"derivedFrom":subQ5}),1.0]])]});}
            var Q1;
            {var subQ0=sQuery(id+"F19.wireOp",EDGE,"E91.top");var subQ1=sQuery(id+"F19.wireOp",EDGE,"E87");var subQ2=makeQuery(id+"F19.imprint","INTERSECT",VERTEX,{"derivedFrom":[subQ1,subQ0]});Q1=makeQuery(id+"F19.imprint","IMPRINT",FACE,{"disambiguationData":[TD([[makeQuery(id+"F19.imprint","IMPRINT",EDGE,{"disambiguationData":[TD([[subQ2,-1.0]])],"derivedFrom":subQ1}),-1.0]])]});}
            var Q2;
            {var subQ5=sQuery(id+"F19.wireOp",EDGE,"E91.right");Q2=makeQuery(id+"F19.imprint","IMPRINT",FACE,{"disambiguationData":[TD([[makeQuery(id+"F19.imprint","IMPRINT",EDGE,{"derivedFrom":subQ5}),-1.0]])]});}
            var Q3;
            Q3=sQuery(id+"F19.wireOp",EDGE,"E91.top");
            revolve(context, id + "F20", {"operationType" : NewBodyOperationType.ADD, "entities" : qUnion([Q0, Q1, Q2]), "axis" : qUnion([Q3]), "revolveType" : RevolveType.FULL});
        }
        {
            var Q0;
            {var subQ0=sQuery(id+"F19.wireOp",EDGE,"E82.top");Q0=makeQuery(id+"F19.imprint","IMPRINT",FACE,{"disambiguationData":[TD([[makeQuery(id+"F19.imprint","IMPRINT",EDGE,{"derivedFrom":subQ0}),-1.0]])]});}
            var Q1;
            {var subQ0=sQuery(id+"F19.wireOp",EDGE,"E91.top");var subQ1=sQuery(id+"F19.wireOp",EDGE,"E87");var subQ2=makeQuery(id+"F19.imprint","INTERSECT",VERTEX,{"derivedFrom":[subQ1,subQ0]});Q1=makeQuery(id+"F19.imprint","IMPRINT",FACE,{"disambiguationData":[TD([[makeQuery(id+"F19.imprint","IMPRINT",EDGE,{"disambiguationData":[TD([[subQ2,-1.0]])],"derivedFrom":subQ1}),-1.0]])]});}
            var Q2;
            {var subQ0=sQuery(id+"F19.wireOp",EDGE,"E88");Q2=makeQuery(id+"F19.imprint","IMPRINT",FACE,{"disambiguationData":[TD([[makeQuery(id+"F19.imprint","IMPRINT",EDGE,{"derivedFrom":subQ0}),-1.0]])]});}
            extrude(context, id + "F21", {"entities" : qUnion([Q0, Q1, Q2]), "endBound" : BoundingType.SYMMETRIC, "depth" : 40 * mm, "offsetDistance" : 25 * mm});
        }
        {
            var Q0;
            Q0=makeQuery(id+"F21.opExtrude","SWEPT_FACE",FACE,{"disambiguationData":[OSD([sQuery(id+"F19.wireOp",EDGE,"E89")])]});
            var sketch = newSketch(context, id + "F22", { "sketchPlane" : qUnion([Q0])});
            skPoint(sketch, "E93", {"position": v(0, 15) * mm});
            skSolve(sketch);
        }
        {
            var Q0;
            Q0=sQuery(id+"F22.wireOp",VERTEX,"E93");
            var Q1;
            Q1=makeQuery(id+"F21.opExtrude","SWEPT_BODY",BODY,{"disambiguationData":[OSD([sQuery(id+"F19.wireOp",EDGE,"E82.top"),sQuery(id+"F19.wireOp",EDGE,"E83"),sQuery(id+"F19.wireOp",EDGE,"E84"),sQuery(id+"F19.wireOp",EDGE,"E85"),sQuery(id+"F19.wireOp",EDGE,"E87"),sQuery(id+"F19.wireOp",EDGE,"E88"),sQuery(id+"F19.wireOp",EDGE,"E89"),sQuery(id+"F19.wireOp",EDGE,"E90.trimOffspring")])]});
            hole(context, id + "F23", {"style" : HoleStyle.SIMPLE, "endStyle" : HoleEndStyle.BLIND, "holeDiameter" : 10.5 * mm, "majorDiameter" : 5 * mm, "holeDepth" : 10 * mm, "isTappedThrough" : true, "tappedDepth" : 12 * mm, "tapClearance" : 3, "locations" : qUnion([Q0]), "scope" : qUnion([Q1])});
        }
        {
            var Q0;
            Q0=makeQuery(id+"F21.opExtrude","SWEPT_FACE",FACE,{"disambiguationData":[OSD([sQuery(id+"F19.wireOp",EDGE,"E85")])]});
            var sketch = newSketch(context, id + "F24", { "sketchPlane" : qUnion([Q0])});
            skPoint(sketch, "E94", {"position": v(0, 15) * mm});
            skSolve(sketch);
        }
        {
            var Q0;
            Q0=sQuery(id+"F24.wireOp",VERTEX,"E94");
            var Q1;
            Q1=makeQuery(id+"F21.opExtrude","SWEPT_BODY",BODY,{"disambiguationData":[OSD([sQuery(id+"F19.wireOp",EDGE,"E82.top"),sQuery(id+"F19.wireOp",EDGE,"E83"),sQuery(id+"F19.wireOp",EDGE,"E84"),sQuery(id+"F19.wireOp",EDGE,"E85"),sQuery(id+"F19.wireOp",EDGE,"E87"),sQuery(id+"F19.wireOp",EDGE,"E88"),sQuery(id+"F19.wireOp",EDGE,"E89"),sQuery(id+"F19.wireOp",EDGE,"E90.trimOffspring")])]});
            hole(context, id + "F25", {"style" : HoleStyle.SIMPLE, "endStyle" : HoleEndStyle.BLIND, "holeDiameter" : 10.5 * mm, "majorDiameter" : 5 * mm, "holeDepth" : 30 * mm, "isTappedThrough" : true, "tappedDepth" : 12 * mm, "tapClearance" : 3, "locations" : qUnion([Q0]), "scope" : qUnion([Q1])});
        }
        {
            var Q0;
            Q0=makeQuery(id+"F21.opExtrude","SWEPT_FACE",FACE,{"disambiguationData":[OSD([sQuery(id+"F19.wireOp",EDGE,"E90.trimOffspring")])]});
            var sketch = newSketch(context, id + "F26", { "sketchPlane" : qUnion([Q0])});
            skLineSegment(sketch, "E95.bottom", {"start": v(-10, -67.5) * mm, "end": v(10, -67.5) * mm});
            skLineSegment(sketch, "E95.top", {"start": v(-10, 62.5) * mm, "end": v(10, 62.5) * mm});
            skLineSegment(sketch, "E95.left", {"start": v(-10, -67.5) * mm, "end": v(-10, 62.5) * mm});
            skLineSegment(sketch, "E95.right", {"start": v(10, -67.5) * mm, "end": v(10, 62.5) * mm});
            skSolve(sketch);
        }
        {
            var Q0;
            Q0=makeQuery(id+"F26.imprint","IMPRINT",FACE,{"disambiguationData":[TD([[makeQuery(id+"F26.imprint","IMPRINT",EDGE,{"derivedFrom":sQuery(id+"F26.wireOp",EDGE,"E95.bottom")}),1.0]])]});
            extrude(context, id + "F27", {"entities" : qUnion([Q0]), "operationType" : NewBodyOperationType.REMOVE, "endBound" : BoundingType.UP_TO_NEXT, "oppositeDirection" : true, "depth" : 25 * mm, "offsetDistance" : 25 * mm});
        }
        {
            var Q0;
            Q0=makeQuery(id+"F21.opExtrude","SWEPT_FACE",FACE,{"disambiguationData":[OSD([sQuery(id+"F19.wireOp",EDGE,"E85")])]});
            var sketch = newSketch(context, id + "F28", { "sketchPlane" : qUnion([Q0])});
            skLineSegment(sketch, "E96.bottom", {"start": v(-20, 25) * mm, "end": v(-10, 25) * mm});
            skLineSegment(sketch, "E96.top", {"start": v(-20, -10) * mm, "end": v(-10, -10) * mm});
            skLineSegment(sketch, "E96.left", {"start": v(-20, 25) * mm, "end": v(-20, -10) * mm});
            skLineSegment(sketch, "E96.right", {"start": v(-10, 25) * mm, "end": v(-10, -10) * mm});
            skLineSegment(sketch, "E97.MirrorCS", {"start": v(10, 25) * mm, "end": v(10, -10) * mm});
            skLineSegment(sketch, "E98.MirrorCS", {"start": v(20, 25) * mm, "end": v(10, 25) * mm});
            skLineSegment(sketch, "E99.MirrorCS", {"start": v(20, 25) * mm, "end": v(20, -10) * mm});
            skLineSegment(sketch, "E100.MirrorCS", {"start": v(20, -10) * mm, "end": v(10, -10) * mm});
            skSolve(sketch);
        }
        {
            var Q0;
            Q0=makeQuery(id+"F28.imprint","IMPRINT",FACE,{"disambiguationData":[TD([[makeQuery(id+"F28.imprint","IMPRINT",EDGE,{"derivedFrom":sQuery(id+"F28.wireOp",EDGE,"E96.bottom")}),1.0]])]});
            var Q1;
            Q1=makeQuery(id+"F28.imprint","IMPRINT",FACE,{"disambiguationData":[TD([[makeQuery(id+"F28.imprint","IMPRINT",EDGE,{"derivedFrom":sQuery(id+"F28.wireOp",EDGE,"E97.MirrorCS")}),1.0]])]});
            extrude(context, id + "F29", {"entities" : qUnion([Q0, Q1]), "operationType" : NewBodyOperationType.REMOVE, "endBound" : BoundingType.THROUGH_ALL, "oppositeDirection" : true, "depth" : 25 * mm, "offsetDistance" : 25 * mm});
        }
    });
